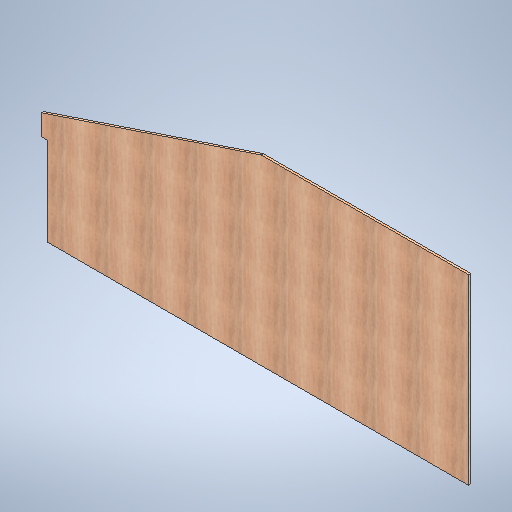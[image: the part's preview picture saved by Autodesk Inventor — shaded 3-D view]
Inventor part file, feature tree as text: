
AUTODESK INVENTOR PART (.ipt)
format: ipt  version: 2025.1 (Build 291241020, 241B)  size: 368,128 bytes
history: native  units: in
note: dims shown in document units (in); Inventor stores cm internally (conversion verified against a paired STEP export)
features: extrude x1, sketch x1
ambient origin geometry x8: Origin, YZ Plane, XZ Plane, XY Plane, X Axis, Y Axis, Z Axis, Center Point
bodies: Solid1 (feature_tree)
feature tree (2):
  extrude  "Extrusion1"  Depth=0.5in
  sketch  "Sketch1"  dims[d1=24.294in d3=0.5in d4=132.0in d6=5.5in d8=3.5in d9=42.875in d10=0.5in d11=0.0in d12=1.8815in d14=0.625in d16=48.0in d18=95.944in]
